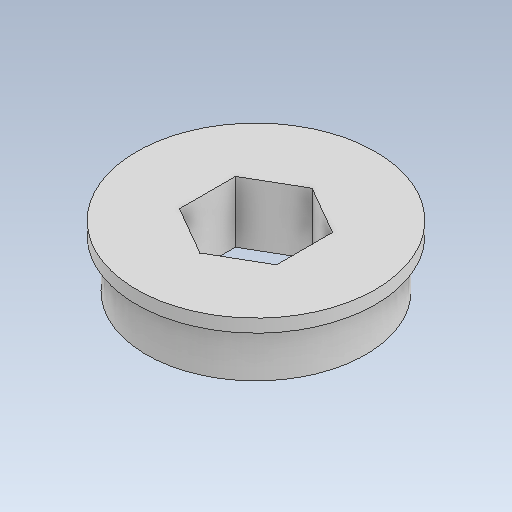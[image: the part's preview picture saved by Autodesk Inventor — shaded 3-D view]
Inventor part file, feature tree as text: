
AUTODESK INVENTOR PART (.ipt)
format: ipt  version: 2023 (Build 270158000, 158)  size: 119,808 bytes
history: native  units: in
note: dims shown in document units (in); Inventor stores cm internally (conversion verified against a paired STEP export)
features: extrude x2, sketch x2
ambient origin geometry x8: Origin, YZ Plane, XZ Plane, XY Plane, X Axis, Y Axis, Z Axis, Center Point
bodies: Solid1 (feature_tree)
feature tree (4):
  extrude  "Extrusion1"  Depth=0.2494in
  extrude  "Extrusion2"  Depth=0.0669in
  sketch  "Sketch1"  dims[d0=1.1268in d1=0.2494in]
  sketch  "Sketch2"  dims[d2=0.315in d3=0.0in d4=1.2272in d5=0.0669in d6=0.0in]
